# Revit family: 3034817 Sylvania Lighting Fixture GIOTTO335 LED G2 3000K SURFACE EMERGENCY
name_source: partatom
category: Lighting Fixtures
revit_build: Autodesk Revit 2016 (Build: 20150220_1215(x64)
units: mm (PartAtom-declared; Revit-internal decimal feet)

## family parameters
Cut with Voids When Loaded = No
Host = Face
Light Source = Yes
OmniClass Number = 23.80.70.00
OmniClass Title = Lighting
Part Type = Normal
Room Calculation Point = No
Round Connector Dimension = Use Diameter
Shared = No

## types (2) — shared parameters
Assembly Code = D5020200
AssetType = Fixed
ClassificationName = Uniclass2015
ClassificationValue = EF_70_80
Color Filter = 16777215
Default Elevation = 1219 mm
Description = Ambient and decorative round, surface mounted LED bulkhead luminaire. White robust polycarbonate body with opal diffuser, 2056 lm, 24W, 86lm/W, 3000K, CRI 80, non-dimmable, integral 3 hour maintained emergency, 50,000 hours lumen maintenance. Drive current: 700mA, IP44, IK10, Class I, 220-240V, Energy class: A++, A+, A.
Diameter_SYL = 335 mm  [stored 1.09908 ft]
DiffuserRadius_SYL = 283 mm
Dimming Lamp Color Temperature Shift = <None>
DocumentationLiterature = http://www.sylvania-lighting.com
DurationUnit = hours
ElectricShockClassification = Class I
Emit Shape Visible in Rendering = No
Emit from Circle Diameter = 317 mm  [stored 1.04003 ft]
ExpectedLife = 50000
Height_SYL = 110 mm  [stored 0.360892 ft]
IfcExportAs = IfcLightFixtureType
IfcExportType = IfcLightFixtureType
ImpactProtectionIndex = IK10
IngressProtection = IP44
Keynote = 16500
Lamp = LED
LampColourRenderingIndex = 80
LampColourTemperature = 3000 K
LampNominalLuminous = 2056 lm
LampsType = LED
LuminousEfficacy = 86 lm/W
Manufacturer = Feilo Sylvania
ManufacturerName = Feilo Sylvania
Material = polycarbonate housing, polycarbonate diffuser
Material_1_SYL = Polycarbonate_Sylvania_Giotto_White
Material_2_SYL = Polycarbonate_Sylvania_Giotto_Opal
Material_3_SYL = LED-Sylvania
Material_4_SYL = <By Category>
Model = GIOTTO335 LED G2 3000K SURFACE EMERGENCY
ModelNumber = 3034817
ModelReference = GIOTTO335 LED G2 3000K SURFACE EMERGENCY
Name = GIOTTO335 LED G2 3000K SURFACE EMERGENCY
NominalDepth = 335 mm  [stored 1.09908 ft]
NominalHeight = 110 mm  [stored 0.360892 ft]
NominalLength = 335 mm  [stored 1.09908 ft]
PowerConsumption = 24 W
Tilt Angle = -90.00°
Type Image = <None>
TypeName = GIOTTO335 LED G2 3000K SURFACE EMERGENCY
URL = http://www.sylvania-lighting.com
Voltage = 230 V
Weight = 1.5 kg
zero-valued in all types: Cost, PowerFactor

## per-type parameters (varying)
| type | Apparent Load | Photometric Web File |
| 3034817 GIOTTO335 LED G2 SURFACE 3000K E3 | 24 VA | 3034817.ies |
| 3034817 GIOTTO335 LED G2 SURFACE 3000K E3 Emergency mode | 1 VA | 3034817EM.ies |

note: [stored X ft] marks values corroborated as IEEE doubles in the binary element streams (Revit-internal decimal feet)

## geometry (parser evidence)
native form markers: Sweep x3
no freeform markers — native parametric forms only
